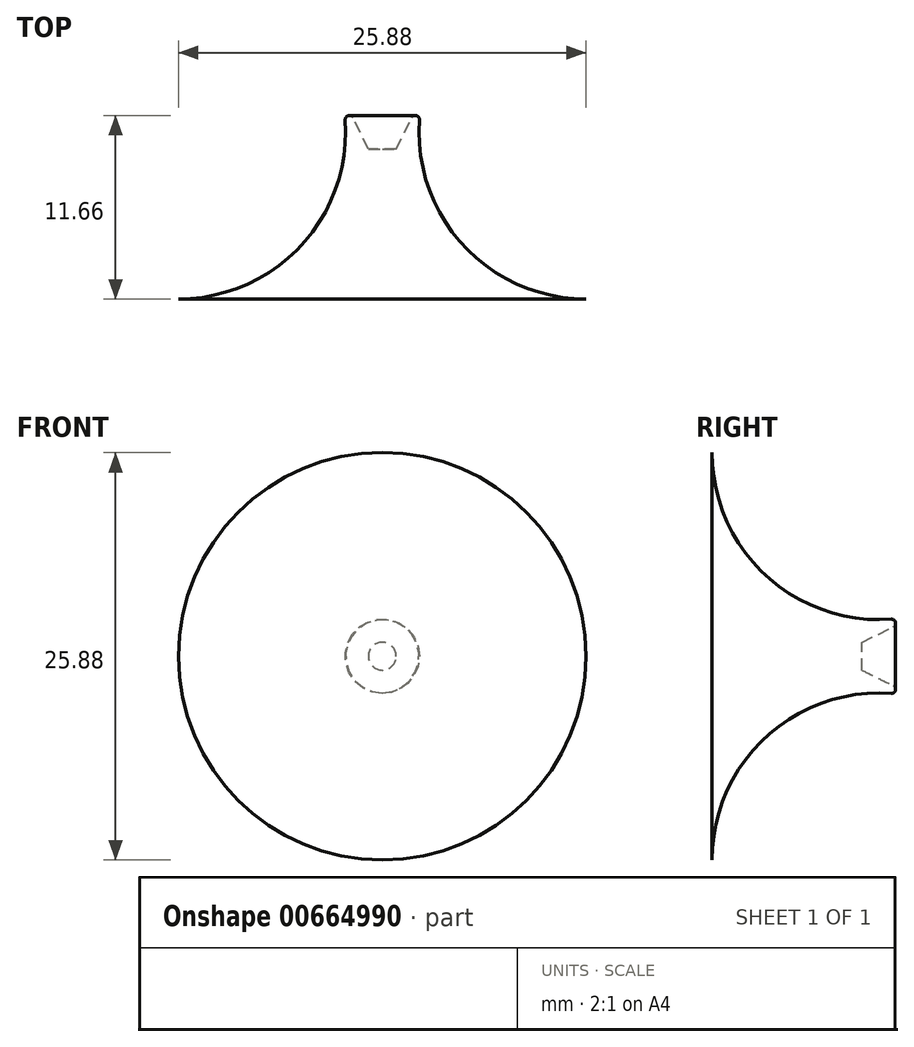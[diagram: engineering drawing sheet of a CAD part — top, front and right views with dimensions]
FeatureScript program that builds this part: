
annotation { "Feature Type Name" : "Feature", "Feature Type Description" : "" }
export const myFeature = defineFeature(function(context is Context, id is Id, definition is map)
    precondition{}
    {
        {
            var Q0;
            Q0=qCreatedBy(makeId("Top.planeOp"),FACE);
            var sketch = newSketch(context, id + "F0", { "sketchPlane" : qUnion([Q0])});
            skLineSegment(sketch, "E0", {"start": v(0, 0) * mm, "end": v(-12.94, 0) * mm});
            skArc(sketch, "E1", {"start": v(-12.94, 0) * mm, "mid": v(-4.65, 3.98) * mm, "end": v(-2.59, 12.94) * mm});
            skLineSegment(sketch, "E2", {"start": v(-1.3, 10.35) * mm, "end": v(-2.59, 12.94) * mm});
            skPoint(sketch, "E3.orphan", {"position": v(0, 12.94) * mm});
            skLineSegment(sketch, "E4", {"start": v(0, 0) * mm, "end": v(0, 9.53) * mm});
            skLineSegment(sketch, "E5", {"start": v(-1.3, 10.35) * mm, "end": v(-0.88, 9.53) * mm});
            skLineSegment(sketch, "E6", {"start": v(-0.88, 9.53) * mm, "end": v(0, 9.53) * mm});
            skSolve(sketch);
        }
        {
            var Q0;
            Q0=makeQuery(id+"F0.imprint","IMPRINT",FACE,{"disambiguationData":[TD([[makeQuery(id+"F0.imprint","IMPRINT",EDGE,{"derivedFrom":sQuery(id+"F0.wireOp",EDGE,"E0")}),-1.0]])]});
            var Q1;
            Q1=sQuery(id+"F0.wireOp",EDGE,"E4");
            revolve(context, id + "F1", {"entities" : qUnion([Q0]), "axis" : qUnion([Q1]), "revolveType" : RevolveType.FULL});
        }
        {
            var Q0;
            Q0=makeQuery(id+"F1.opRevolve","SWEPT_EDGE",EDGE,{"disambiguationData":[OSD([sQuery(id+"F0.wireOp",EDGE,"E1"),sQuery(id+"F0.wireOp",EDGE,"E2")])]});
            fillet(context, id + "F2", {"entities" : qUnion([Q0]), "radius" : 0.25 * mm, "tangentPropagation" : true, "allowEdgeOverflow" : false});
        }
    });
